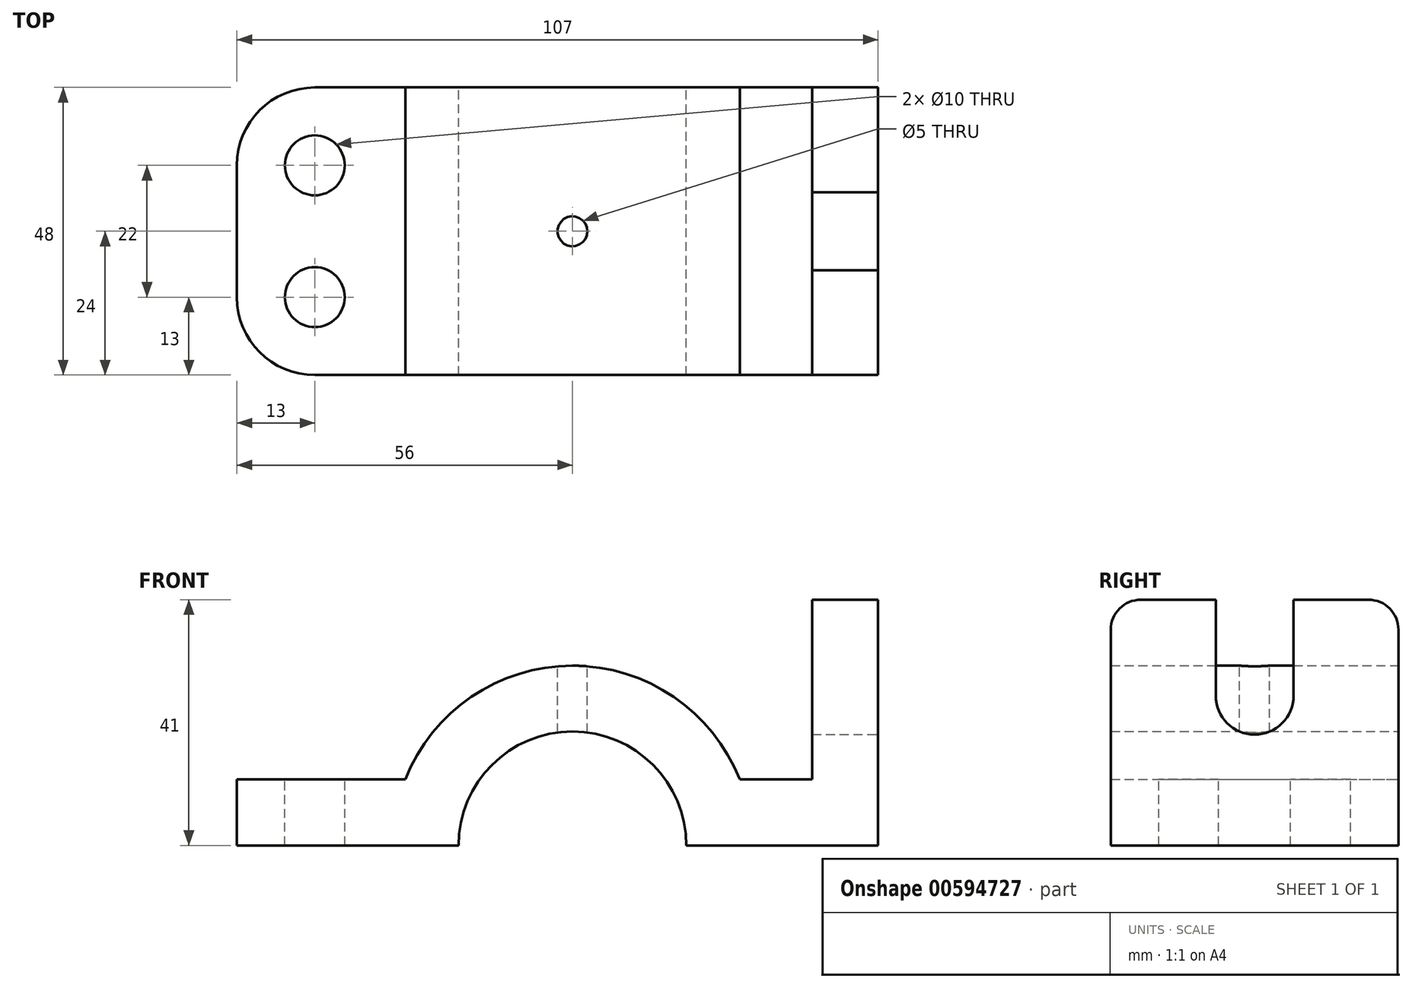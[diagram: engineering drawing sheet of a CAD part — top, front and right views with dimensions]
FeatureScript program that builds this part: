
annotation { "Feature Type Name" : "Feature", "Feature Type Description" : "" }
export const myFeature = defineFeature(function(context is Context, id is Id, definition is map)
    precondition{}
    {
        {
            var Q0;
            Q0=qCreatedBy(makeId("Front.planeOp"),FACE);
            var sketch = newSketch(context, id + "F0", { "sketchPlane" : qUnion([Q0])});
            skLineSegment(sketch, "E0", {"start": v(51, 0) * mm, "end": v(51, 41) * mm});
            skArc(sketch, "E1", {"start": v(19, 0) * mm, "mid": v(0, 19) * mm, "end": v(-19, 0) * mm});
            skLineSegment(sketch, "E2", {"start": v(19, 0) * mm, "end": v(51, 0) * mm});
            skLineSegment(sketch, "E3", {"start": v(-19, 0) * mm, "end": v(-56, 0) * mm});
            skLineSegment(sketch, "E4", {"start": v(-56, 0) * mm, "end": v(-56, 11) * mm});
            skArc(sketch, "E5", {"start": v(27.91, 11) * mm, "mid": v(0, 30) * mm, "end": v(-27.91, 11) * mm});
            skLineSegment(sketch, "E6", {"start": v(-27.91, 11) * mm, "end": v(-56, 11) * mm});
            skLineSegment(sketch, "E7", {"start": v(51, 41) * mm, "end": v(40, 41) * mm});
            skLineSegment(sketch, "E8", {"start": v(40, 41) * mm, "end": v(40, 11) * mm});
            skLineSegment(sketch, "E9", {"start": v(40, 11) * mm, "end": v(27.91, 11) * mm});
            skSolve(sketch);
        }
        {
            var Q0;
            Q0=makeQuery(id+"F0.imprint","IMPRINT",FACE,{"disambiguationData":[TD([[makeQuery(id+"F0.imprint","IMPRINT",EDGE,{"derivedFrom":sQuery(id+"F0.wireOp",EDGE,"E0")}),1.0]])]});
            extrude(context, id + "F1", {"entities" : qUnion([Q0]), "endBound" : BoundingType.SYMMETRIC, "depth" : 48 * mm, "offsetDistance" : 25.4 * mm});
        }
        {
            var Q0;
            Q0=makeQuery(id+"F1.opExtrude","SWEPT_FACE",FACE,{"disambiguationData":[OSD([sQuery(id+"F0.wireOp",EDGE,"E0")])]});
            var sketch = newSketch(context, id + "F2", { "sketchPlane" : qUnion([Q0])});
            skLineSegment(sketch, "E10.0", {"start": v(-24, 41) * mm, "end": v(24, 41) * mm});
            skLineSegment(sketch, "E10.1", {"start": v(24, 0) * mm, "end": v(24, 41) * mm});
            skLineSegment(sketch, "E10.2", {"start": v(-24, 0) * mm, "end": v(24, 0) * mm});
            skLineSegment(sketch, "E10.3", {"start": v(-24, 0) * mm, "end": v(-24, 41) * mm});
            skPoint(sketch, "E10.4", {"position": v(0, 41) * mm});
            skCircle(sketch, "E11", {"center": v(0, 25) * mm, "radius": 6.5 * mm});
            skLineSegment(sketch, "E12", {"start": v(-6.5, 25) * mm, "end": v(-6.5, 41) * mm});
            skLineSegment(sketch, "E13", {"start": v(-6.5, 41) * mm, "end": v(6.5, 41) * mm});
            skLineSegment(sketch, "E14", {"start": v(6.5, 41) * mm, "end": v(6.5, 25) * mm});
            skSolve(sketch);
        }
        {
            var Q0;
            {var subQ0=sQuery(id+"F2.wireOp",EDGE,"E11");var subQ1=makeQuery(id+"F2.imprint","INTERSECT",VERTEX,{"derivedFrom":[subQ0,sQuery(id+"F2.wireOp",EDGE,"E12")]});Q0=makeQuery(id+"F2.imprint","IMPRINT",FACE,{"disambiguationData":[TD([[makeQuery(id+"F2.imprint","IMPRINT",EDGE,{"disambiguationData":[TD([[subQ1,1.0]])],"derivedFrom":subQ0}),1.0]])]});}
            var Q1;
            {var subQ0=sQuery(id+"F2.wireOp",EDGE,"E12");Q1=makeQuery(id+"F2.imprint","IMPRINT",FACE,{"disambiguationData":[TD([[makeQuery(id+"F2.imprint","IMPRINT",EDGE,{"derivedFrom":subQ0}),-1.0]])]});}
            var Q2;
            Q2=makeQuery(id+"F1.opExtrude","SWEPT_FACE",FACE,{"disambiguationData":[OSD([sQuery(id+"F0.wireOp",EDGE,"E8")])]});
            extrude(context, id + "F3", {"entities" : qUnion([Q0, Q1]), "operationType" : NewBodyOperationType.REMOVE, "endBound" : BoundingType.UP_TO_SURFACE, "oppositeDirection" : true, "depth" : 25.4 * mm, "endBoundEntityFace" : qUnion([Q2]), "offsetDistance" : 25.4 * mm});
        }
        {
            var Q0;
            Q0=makeQuery(id+"F1.opExtrude","SWEPT_FACE",FACE,{"disambiguationData":[OSD([sQuery(id+"F0.wireOp",EDGE,"E6")])]});
            var sketch = newSketch(context, id + "F4", { "sketchPlane" : qUnion([Q0])});
            skCircle(sketch, "E15", {"center": v(-43, 11) * mm, "radius": 5 * mm});
            skCircle(sketch, "E16", {"center": v(-43, -11) * mm, "radius": 5 * mm});
            skCircle(sketch, "E17", {"center": v(0, 0) * mm, "radius": 2.5 * mm});
            skSolve(sketch);
        }
        {
            var Q0;
            Q0=makeQuery(id+"F1.opExtrude","CAP_EDGE",EDGE,{"disambiguationData":[OSD([sQuery(id+"F0.wireOp",EDGE,"E4")])],"isStart":false});
            var Q1;
            Q1=makeQuery(id+"F1.opExtrude","CAP_EDGE",EDGE,{"disambiguationData":[OSD([sQuery(id+"F0.wireOp",EDGE,"E4")])],"isStart":true});
            fillet(context, id + "F5", {"entities" : qUnion([Q0, Q1]), "radius" : 13 * mm, "tangentPropagation" : true, "allowEdgeOverflow" : false});
        }
        {
            var Q0;
            Q0=makeQuery(id+"F1.opExtrude","CAP_EDGE",EDGE,{"disambiguationData":[OSD([sQuery(id+"F0.wireOp",EDGE,"E7")])],"isStart":false});
            var Q1;
            Q1=makeQuery(id+"F1.opExtrude","CAP_EDGE",EDGE,{"disambiguationData":[OSD([sQuery(id+"F0.wireOp",EDGE,"E7")])],"isStart":true});
            fillet(context, id + "F6", {"entities" : qUnion([Q0, Q1]), "radius" : 5 * mm, "tangentPropagation" : true, "allowEdgeOverflow" : false});
        }
        {
            var Q0;
            Q0=makeQuery(id+"F4.imprint","IMPRINT",FACE,{"disambiguationData":[TD([[makeQuery(id+"F4.imprint","IMPRINT",EDGE,{"derivedFrom":sQuery(id+"F4.wireOp",EDGE,"E17")}),1.0]])]});
            var Q1;
            Q1=makeQuery(id+"F4.imprint","IMPRINT",FACE,{"disambiguationData":[TD([[makeQuery(id+"F4.imprint","IMPRINT",EDGE,{"derivedFrom":sQuery(id+"F4.wireOp",EDGE,"E16")}),1.0]])]});
            var Q2;
            Q2=makeQuery(id+"F4.imprint","IMPRINT",FACE,{"disambiguationData":[TD([[makeQuery(id+"F4.imprint","IMPRINT",EDGE,{"derivedFrom":sQuery(id+"F4.wireOp",EDGE,"E15")}),1.0]])]});
            extrude(context, id + "F7", {"entities" : qUnion([Q0, Q1, Q2]), "operationType" : NewBodyOperationType.REMOVE, "endBound" : BoundingType.SYMMETRIC, "oppositeDirection" : true, "depth" : 76.2 * mm, "offsetDistance" : 25.4 * mm});
        }
    });
